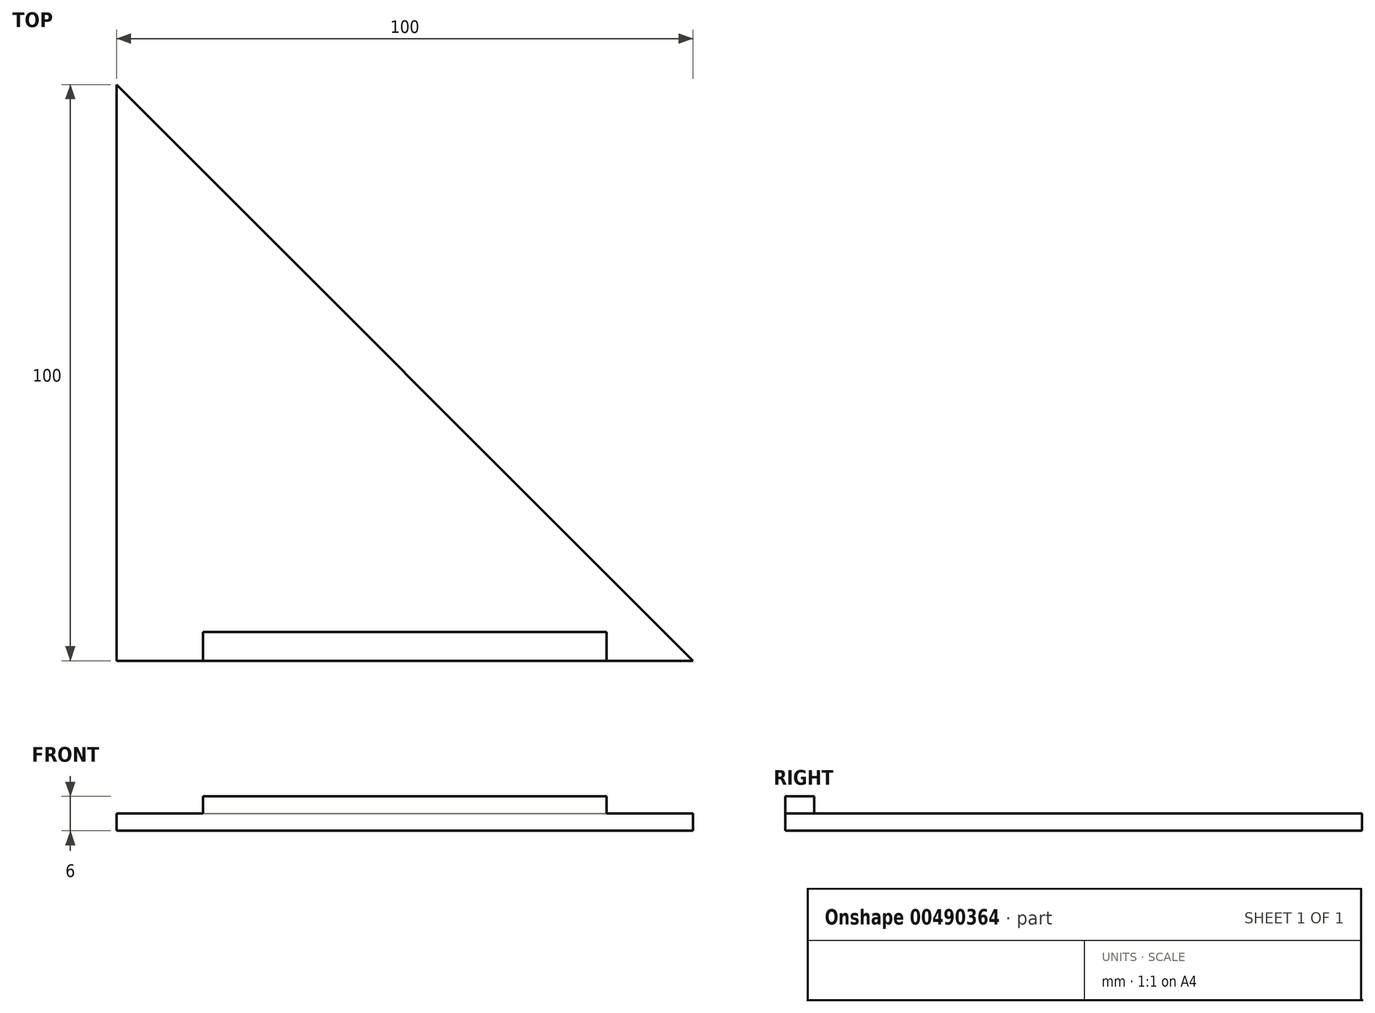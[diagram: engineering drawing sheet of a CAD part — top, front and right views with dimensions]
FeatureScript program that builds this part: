
annotation { "Feature Type Name" : "Feature", "Feature Type Description" : "" }
export const myFeature = defineFeature(function(context is Context, id is Id, definition is map)
    precondition{}
    {
        {
            var Q0;
            Q0=qCreatedBy(makeId("Top.planeOp"),FACE);
            var sketch = newSketch(context, id + "F0", { "sketchPlane" : qUnion([Q0])});
            skLineSegment(sketch, "E0.bottom", {"start": v(0, 0) * mm, "end": v(100, 0) * mm});
            skLineSegment(sketch, "E0.left", {"start": v(0, 0) * mm, "end": v(0, 100) * mm});
            skLineSegment(sketch, "E1", {"start": v(0, 100) * mm, "end": v(100, 0) * mm});
            skSolve(sketch);
        }
        {
            var Q0;
            Q0 = qSketchRegion(id + "F0", true);
            extrude(context, id + "F1", {"entities" : qUnion([Q0]), "depth" : 3 * mm});
        }
        {
            var Q0;
            Q0=makeQuery(id+"F1.opExtrude","CAP_FACE",FACE,{"disambiguationData":[OSD([sQuery(id+"F0.wireOp",EDGE,"E0.bottom"),sQuery(id+"F0.wireOp",EDGE,"E0.left"),sQuery(id+"F0.wireOp",EDGE,"E1")])],"isStart":false});
            var sketch = newSketch(context, id + "F2", { "sketchPlane" : qUnion([Q0])});
            skLineSegment(sketch, "E2.bottom", {"start": v(15, 0) * mm, "end": v(85, 0) * mm});
            skLineSegment(sketch, "E2.top", {"start": v(15, 5) * mm, "end": v(85, 5) * mm});
            skLineSegment(sketch, "E2.left", {"start": v(15, 0) * mm, "end": v(15, 5) * mm});
            skLineSegment(sketch, "E2.right", {"start": v(85, 0) * mm, "end": v(85, 5) * mm});
            skSolve(sketch);
        }
        {
            var Q0;
            Q0 = qSketchRegion(id + "F2", true);
            extrude(context, id + "F3", {"entities" : qUnion([Q0]), "operationType" : NewBodyOperationType.ADD, "depth" : 3 * mm});
        }
    });
